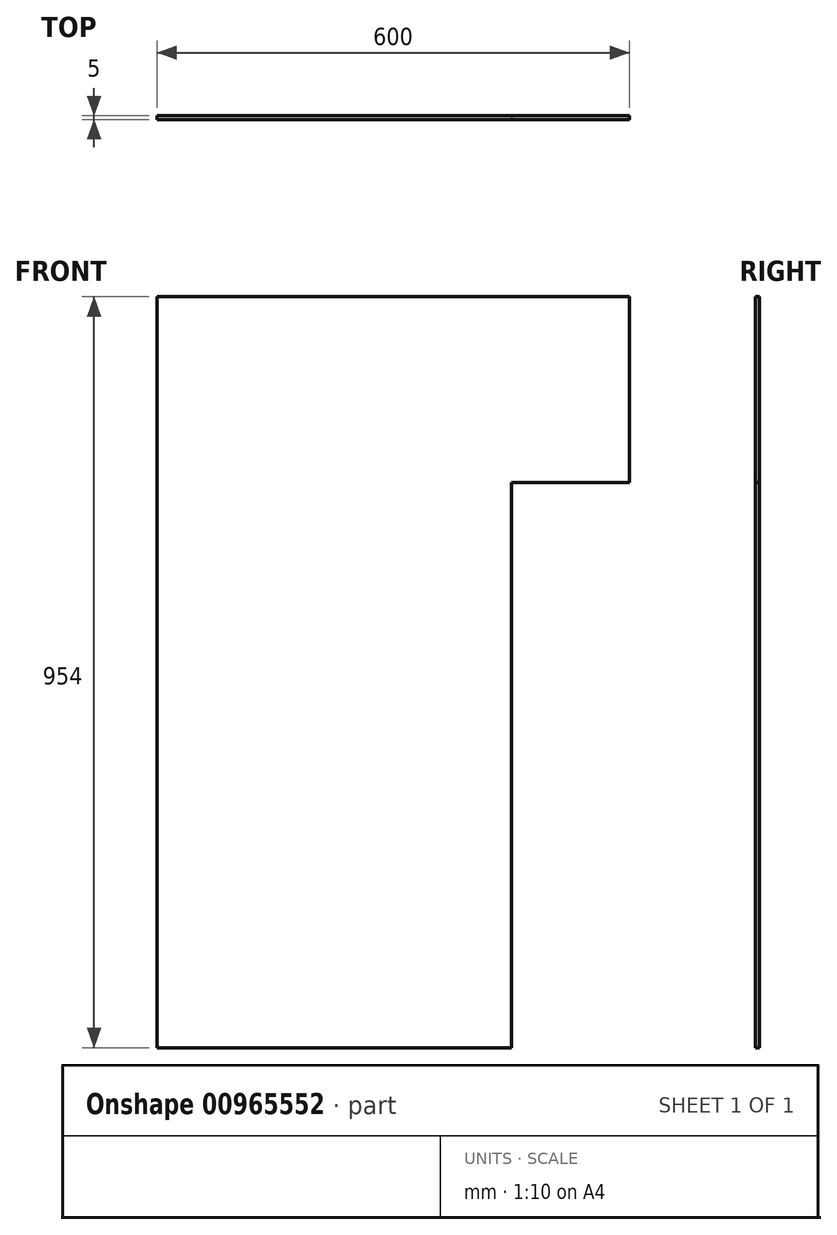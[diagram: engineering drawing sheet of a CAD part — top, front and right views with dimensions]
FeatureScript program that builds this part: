
annotation { "Feature Type Name" : "Feature", "Feature Type Description" : "" }
export const myFeature = defineFeature(function(context is Context, id is Id, definition is map)
    precondition{}
    {
        {
            var Q0;
            Q0=qCreatedBy(makeId("Front.planeOp"),FACE);
            var sketch = newSketch(context, id + "F0", { "sketchPlane" : qUnion([Q0])});
            skLineSegment(sketch, "E0.bottom", {"start": v(300, 477) * mm, "end": v(-300, 477) * mm});
            skLineSegment(sketch, "E0.top", {"start": v(300, -477) * mm, "end": v(-300, -477) * mm});
            skLineSegment(sketch, "E0.left", {"start": v(300, 477) * mm, "end": v(300, -477) * mm});
            skLineSegment(sketch, "E0.right", {"start": v(-300, 477) * mm, "end": v(-300, -477) * mm});
            skPoint(sketch, "E0.middle", {"position": v(0, 0) * mm});
            skSolve(sketch);
        }
        {
            var Q0;
            Q0=makeQuery(id+"F0.imprint","IMPRINT",FACE,{"disambiguationData":[TD([[makeQuery(id+"F0.imprint","IMPRINT",EDGE,{"derivedFrom":sQuery(id+"F0.wireOp",EDGE,"E0.bottom")}),1.0]])]});
            extrude(context, id + "F1", {"entities" : qUnion([Q0]), "depth" : 5 * mm, "offsetDistance" : 25 * mm});
        }
        {
            var Q0;
            Q0=makeQuery(id+"F1.opExtrude","CAP_FACE",FACE,{"disambiguationData":[OSD([sQuery(id+"F0.wireOp",EDGE,"E0.bottom"),sQuery(id+"F0.wireOp",EDGE,"E0.top"),sQuery(id+"F0.wireOp",EDGE,"E0.left"),sQuery(id+"F0.wireOp",EDGE,"E0.right")])],"isStart":false});
            var sketch = newSketch(context, id + "F2", { "sketchPlane" : qUnion([Q0])});
            skLineSegment(sketch, "E1.bottom", {"start": v(300, -477) * mm, "end": v(150, -477) * mm});
            skLineSegment(sketch, "E1.top", {"start": v(300, 241) * mm, "end": v(150, 241) * mm});
            skLineSegment(sketch, "E1.left", {"start": v(300, -477) * mm, "end": v(300, 241) * mm});
            skLineSegment(sketch, "E1.right", {"start": v(150, -477) * mm, "end": v(150, 241) * mm});
            skSolve(sketch);
        }
        {
            var Q0;
            Q0=makeQuery(id+"F2.imprint","IMPRINT",FACE,{"disambiguationData":[TD([[makeQuery(id+"F2.imprint","IMPRINT",EDGE,{"derivedFrom":sQuery(id+"F2.wireOp",EDGE,"E1.bottom")}),-1.0]])]});
            extrude(context, id + "F3", {"entities" : qUnion([Q0]), "operationType" : NewBodyOperationType.REMOVE, "endBound" : BoundingType.THROUGH_ALL, "oppositeDirection" : true, "depth" : 25 * mm, "offsetDistance" : 25 * mm});
        }
    });
